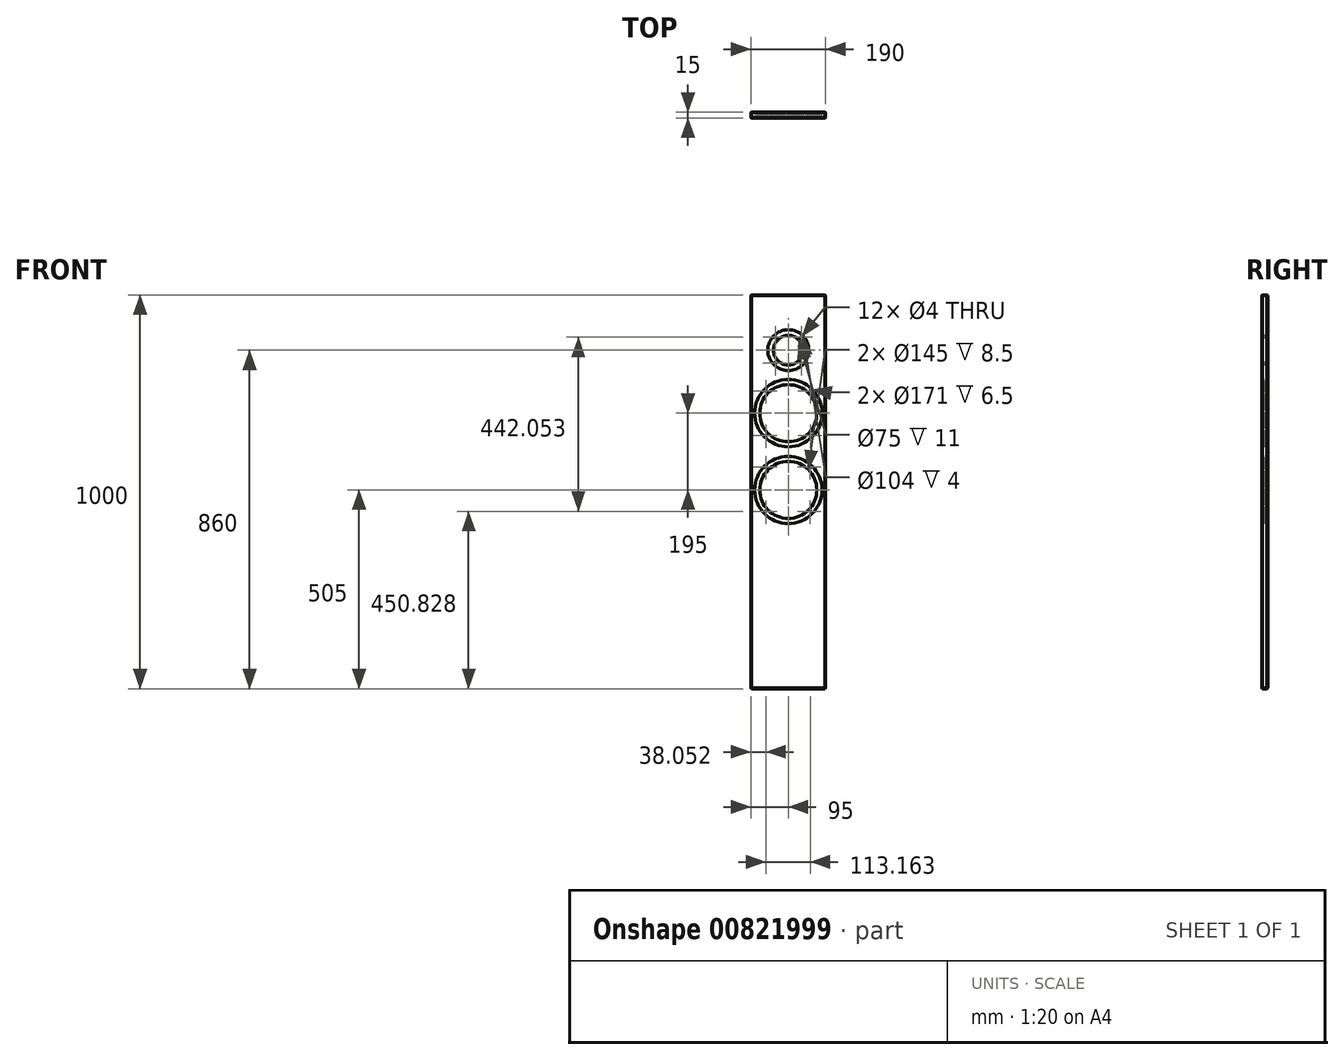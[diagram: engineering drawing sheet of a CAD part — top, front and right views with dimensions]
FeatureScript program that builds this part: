
annotation { "Feature Type Name" : "Feature", "Feature Type Description" : "" }
export const myFeature = defineFeature(function(context is Context, id is Id, definition is map)
    precondition{}
    {
        {
            var Q0;
            Q0=qCreatedBy(makeId("Front.planeOp"),FACE);
            var sketch = newSketch(context, id + "F0", { "sketchPlane" : qUnion([Q0])});
            skLineSegment(sketch, "E0.bottom", {"start": v(-95, -500) * mm, "end": v(95, -500) * mm});
            skLineSegment(sketch, "E0.top", {"start": v(-95, 500) * mm, "end": v(95, 500) * mm});
            skLineSegment(sketch, "E0.left", {"start": v(-95, -500) * mm, "end": v(-95, 500) * mm});
            skLineSegment(sketch, "E0.right", {"start": v(95, -500) * mm, "end": v(95, 500) * mm});
            skPoint(sketch, "E1", {"position": v(0, 360) * mm});
            skPoint(sketch, "E2", {"position": v(0, 200) * mm});
            skPoint(sketch, "E3", {"position": v(0, 5) * mm});
            skPoint(sketch, "E4", {"position": v(56.21, 256.21) * mm});
            skPoint(sketch, "E5.1.0", {"position": v(-56.21, 256.21) * mm});
            skPoint(sketch, "E5.2.0", {"position": v(-56.21, 143.79) * mm});
            skPoint(sketch, "E5.3.0", {"position": v(56.21, 143.79) * mm});
            skLineSegment(sketch, "E6.0", {"start": v(0, 200) * mm, "end": v(0, 200) * mm});
            skLineSegment(sketch, "E6.1", {"start": v(0, 200) * mm, "end": v(56.21, 256.21) * mm, "construction": true});
            skPoint(sketch, "E7", {"position": v(55.48, 63.26) * mm});
            skPoint(sketch, "E8.1.0", {"position": v(-56.95, 63.26) * mm});
            skPoint(sketch, "E8.2.0", {"position": v(-56.95, -49.17) * mm});
            skPoint(sketch, "E8.3.0", {"position": v(55.48, -49.17) * mm});
            skPoint(sketch, "E9", {"position": v(32.88, 392.88) * mm});
            skPoint(sketch, "E10.1.0", {"position": v(-32.88, 392.88) * mm});
            skPoint(sketch, "E10.2.0", {"position": v(-32.88, 327.12) * mm});
            skPoint(sketch, "E10.3.0", {"position": v(32.88, 327.12) * mm});
            skSolve(sketch);
        }
        {
            var Q0;
            Q0=makeQuery(id+"F0.imprint","IMPRINT",FACE,{"disambiguationData":[TD([[makeQuery(id+"F0.imprint","IMPRINT",EDGE,{"derivedFrom":sQuery(id+"F0.wireOp",EDGE,"E0.bottom")}),1.0]])]});
            extrude(context, id + "F1", {"entities" : qUnion([Q0]), "oppositeDirection" : true, "depth" : 15 * mm, "offsetDistance" : 25 * mm});
        }
        {
            var Q0;
            Q0=sQuery(id+"F0.wireOp",VERTEX,"E1");
            var Q1;
            Q1=makeQuery(id+"F1.opExtrude","SWEPT_BODY",BODY,{"disambiguationData":[OSD([sQuery(id+"F0.wireOp",EDGE,"E0.bottom"),sQuery(id+"F0.wireOp",EDGE,"E0.top"),sQuery(id+"F0.wireOp",EDGE,"E0.left"),sQuery(id+"F0.wireOp",EDGE,"E0.right")])]});
            hole(context, id + "F2", {"style" : HoleStyle.C_BORE, "endStyle" : HoleEndStyle.BLIND, "holeDiameter" : 75 * mm, "cBoreDiameter" : 104 * mm, "cBoreDepth" : 4 * mm, "majorDiameter" : 5 * mm, "holeDepth" : 15 * mm, "isTappedThrough" : true, "tappedDepth" : 12 * mm, "tapClearance" : 3, "locations" : qUnion([Q0]), "scope" : qUnion([Q1])});
        }
        {
            var Q0;
            Q0=sQuery(id+"F0.wireOp",VERTEX,"E2");
            var Q1;
            Q1=makeQuery(id+"F1.opExtrude","SWEPT_BODY",BODY,{"disambiguationData":[OSD([sQuery(id+"F0.wireOp",EDGE,"E0.bottom"),sQuery(id+"F0.wireOp",EDGE,"E0.top"),sQuery(id+"F0.wireOp",EDGE,"E0.left"),sQuery(id+"F0.wireOp",EDGE,"E0.right")])]});
            hole(context, id + "F3", {"style" : HoleStyle.C_BORE, "endStyle" : HoleEndStyle.BLIND, "holeDiameter" : 145 * mm, "cBoreDiameter" : 171 * mm, "cBoreDepth" : 6.5 * mm, "majorDiameter" : 5 * mm, "holeDepth" : 15 * mm, "isTappedThrough" : true, "tappedDepth" : 12 * mm, "tapClearance" : 3, "locations" : qUnion([Q0]), "scope" : qUnion([Q1])});
        }
        {
            var Q0;
            Q0=sQuery(id+"F0.wireOp",VERTEX,"E3");
            var Q1;
            Q1=makeQuery(id+"F1.opExtrude","SWEPT_BODY",BODY,{"disambiguationData":[OSD([sQuery(id+"F0.wireOp",EDGE,"E0.bottom"),sQuery(id+"F0.wireOp",EDGE,"E0.top"),sQuery(id+"F0.wireOp",EDGE,"E0.left"),sQuery(id+"F0.wireOp",EDGE,"E0.right")])]});
            hole(context, id + "F4", {"style" : HoleStyle.C_BORE, "endStyle" : HoleEndStyle.BLIND, "holeDiameter" : 145 * mm, "cBoreDiameter" : 171 * mm, "cBoreDepth" : 6.5 * mm, "majorDiameter" : 5 * mm, "holeDepth" : 15 * mm, "isTappedThrough" : true, "tappedDepth" : 12 * mm, "tapClearance" : 3, "locations" : qUnion([Q0]), "scope" : qUnion([Q1])});
        }
        {
            var Q0;
            Q0=sQuery(id+"F0.wireOp",VERTEX,"E5.1.0");
            var Q1;
            Q1=sQuery(id+"F0.wireOp",VERTEX,"E4");
            var Q2;
            Q2=sQuery(id+"F0.wireOp",VERTEX,"E5.3.0");
            var Q3;
            Q3=sQuery(id+"F0.wireOp",VERTEX,"E5.2.0");
            var Q4;
            Q4=sQuery(id+"F0.wireOp",VERTEX,"E8.1.0");
            var Q5;
            Q5=sQuery(id+"F0.wireOp",VERTEX,"E7");
            var Q6;
            Q6=sQuery(id+"F0.wireOp",VERTEX,"E8.3.0");
            var Q7;
            Q7=sQuery(id+"F0.wireOp",VERTEX,"E8.2.0");
            var Q8;
            Q8=sQuery(id+"F0.wireOp",VERTEX,"E10.1.0");
            var Q9;
            Q9=sQuery(id+"F0.wireOp",VERTEX,"E9");
            var Q10;
            Q10=sQuery(id+"F0.wireOp",VERTEX,"E10.3.0");
            var Q11;
            Q11=sQuery(id+"F0.wireOp",VERTEX,"E10.2.0");
            var Q12;
            Q12=makeQuery(id+"F1.opExtrude","SWEPT_BODY",BODY,{"disambiguationData":[OSD([sQuery(id+"F0.wireOp",EDGE,"E0.bottom"),sQuery(id+"F0.wireOp",EDGE,"E0.top"),sQuery(id+"F0.wireOp",EDGE,"E0.left"),sQuery(id+"F0.wireOp",EDGE,"E0.right")])]});
            hole(context, id + "F5", {"style" : HoleStyle.SIMPLE, "endStyle" : HoleEndStyle.BLIND, "holeDiameter" : 4 * mm, "majorDiameter" : 5 * mm, "holeDepth" : 15 * mm, "isTappedThrough" : true, "tappedDepth" : 12 * mm, "tapClearance" : 3, "locations" : qUnion([Q0, Q1, Q2, Q3, Q4, Q5, Q6, Q7, Q8, Q9, Q10, Q11]), "scope" : qUnion([Q12])});
        }
        {
            var Q0;
            Q0=makeQuery(id+"F1.opExtrude","CAP_EDGE",EDGE,{"disambiguationData":[OSD([sQuery(id+"F0.wireOp",EDGE,"E0.left")])],"isStart":true});
            var Q1;
            Q1=makeQuery(id+"F1.opExtrude","CAP_EDGE",EDGE,{"disambiguationData":[OSD([sQuery(id+"F0.wireOp",EDGE,"E0.top")])],"isStart":true});
            var Q2;
            Q2=makeQuery(id+"F1.opExtrude","CAP_EDGE",EDGE,{"disambiguationData":[OSD([sQuery(id+"F0.wireOp",EDGE,"E0.right")])],"isStart":true});
            var Q3;
            Q3=makeQuery(id+"F1.opExtrude","CAP_EDGE",EDGE,{"disambiguationData":[OSD([sQuery(id+"F0.wireOp",EDGE,"E0.bottom")])],"isStart":true});
            var Q4;
            Q4=makeQuery(id+"F1.opExtrude","SWEPT_EDGE",EDGE,{"disambiguationData":[OSD([sQuery(id+"F0.wireOp",EDGE,"E0.bottom"),sQuery(id+"F0.wireOp",EDGE,"E0.left")])]});
            var Q5;
            Q5=makeQuery(id+"F1.opExtrude","CAP_EDGE",EDGE,{"disambiguationData":[OSD([sQuery(id+"F0.wireOp",EDGE,"E0.left")])],"isStart":false});
            var Q6;
            Q6=makeQuery(id+"F1.opExtrude","CAP_EDGE",EDGE,{"disambiguationData":[OSD([sQuery(id+"F0.wireOp",EDGE,"E0.bottom")])],"isStart":false});
            var Q7;
            Q7=makeQuery(id+"F1.opExtrude","SWEPT_EDGE",EDGE,{"disambiguationData":[OSD([sQuery(id+"F0.wireOp",EDGE,"E0.bottom"),sQuery(id+"F0.wireOp",EDGE,"E0.right")])]});
            var Q8;
            Q8=makeQuery(id+"F1.opExtrude","CAP_EDGE",EDGE,{"disambiguationData":[OSD([sQuery(id+"F0.wireOp",EDGE,"E0.right")])],"isStart":false});
            var Q9;
            Q9=makeQuery(id+"F1.opExtrude","SWEPT_EDGE",EDGE,{"disambiguationData":[OSD([sQuery(id+"F0.wireOp",EDGE,"E0.top"),sQuery(id+"F0.wireOp",EDGE,"E0.left")])]});
            var Q10;
            Q10=makeQuery(id+"F1.opExtrude","CAP_EDGE",EDGE,{"disambiguationData":[OSD([sQuery(id+"F0.wireOp",EDGE,"E0.top")])],"isStart":false});
            var Q11;
            Q11=makeQuery(id+"F1.opExtrude","SWEPT_EDGE",EDGE,{"disambiguationData":[OSD([sQuery(id+"F0.wireOp",EDGE,"E0.top"),sQuery(id+"F0.wireOp",EDGE,"E0.right")])]});
            chamfer(context, id + "F6", {"entities" : qUnion([Q0, Q1, Q2, Q3, Q4, Q5, Q6, Q7, Q8, Q9, Q10, Q11]), "width" : 1.5 * mm, "tangentPropagation" : true});
        }
    });
